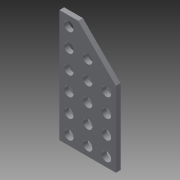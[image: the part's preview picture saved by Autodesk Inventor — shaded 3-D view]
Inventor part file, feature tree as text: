
AUTODESK INVENTOR PART (.ipt)
format: ipt  version: 2013 (Build 170138000, 138)  size: 105,984 bytes
history: native  units: in
note: dims shown in document units (in); Inventor stores cm internally (conversion verified against a paired STEP export)
features: extrude x1, sketch x1
ambient origin geometry x8: Origin, YZ Plane, XZ Plane, XY Plane, X Axis, Y Axis, Z Axis, Center Point
bodies: Solid1 (feature_tree)
feature tree (2):
  extrude  "Extrusion1"  [1 undecoded]
  sketch  "Sketch2"  dims[d1=0.1969in d2=0.0in]
note: 1 required parameter value undecoded (feature->parameter linkage not recoverable at this tier; creation-order binding heuristic only, values carry confidence <= 0.55)
